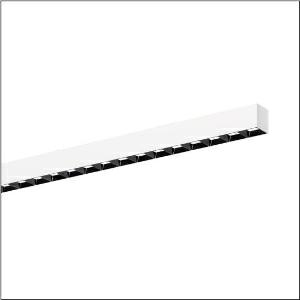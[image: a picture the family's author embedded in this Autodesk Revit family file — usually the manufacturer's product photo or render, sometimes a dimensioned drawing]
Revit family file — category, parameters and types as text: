
# Revit family: silica_r__21_51mx22da44wb_17fd
name_source: partatom
category: Lighting Fixtures
units: mm (PartAtom-declared; Revit-internal decimal feet)

## family parameters
Cut with Voids When Loaded = No
Host = Face
Light Source = No
Part Type = Normal
Room Calculation Point = No
Round Connector Dimension = Use Diameter
Shared = No

## types (1)
- --- (1 x LED, 4320 lm, 25.6 W, 4000K)
    Apparent Load = 26 VA
    CIE Flux Codes = 86 100 100 100 100
    Color Rendering = 80
    Color Temperature = 4000K
    Default Elevation = 1800 mm
    Description = Silica® 21, office luminaire, primary light control with darklight reflector, of PMMA, black, CAT 2 (L<= 3000cd/m²), light emission: direct distribution, primary light characteristic: symmetric, installation type: surface-mounted, LED, rated luminous flux: 4.320lm, luminous efficacy: 169lm/W, light colour: 840, colour temperature: 4000K, with terminal, 3+2-pole, max. 2.5mm², mains connection: 220..240V, AC, 50/60Hz, rated input power: 25.6W, luminaire housing, of aluminium, traffic white (RAL 9016), length: 1.204mm, width: 53mm, height: 53mm, protection rating (complete): IP20, insulation class (complete): insulation class I (protective earthing), certification: CE, permissible operating ambient temperature: 0..+35°C, standard: EN 50419, packaging unit: 1 piece
    Height = 0 mm  [stored 0 ft]
    Lamp = 1 x LED
    Lamp Light Flux = 4320 lm
    Lamp Power = 25.6 W
    Lamp count = 1
    Length = 1204 mm
    Luminous efficacy = 169 lm/W
    Manufacturer = Siteco
    ModVariant = No
    Model = 51MX22DA44WB
    Mounting Place = Ceiling
    Mounting Type = Recessed
    Number of Poles = 1
    OnlyDefault = Yes
    Power Factor = 1
    Product Name = Silica® 21
    Product group = office luminaire | ceiling recessed
    ProductGroupID = 401
    Protection Class = Protection class I
    Protection Degree = IP 20
    RLX_Detail_Level = 1
    RLX_Emergency_Light_Flux = 0 lm
    RLX_Emergency_Type = 0
    RLX_Emergency_Type_DB = No
    RlxData = <blob elided: 41321 chars, md5=b3e29b7a>
    Socket = socket
    Standby Power = 0 W
    System Light Flux = 4320 lm
    System Power = 26 W
    Type Comments = factory setting: luminous flux: 100 % | dim-lin: 254 | 367 mA
    Type Image = l_1313592.jpg
    URL = http://relux.com
    VarID = @adj_074659
    Voltage = 0 V
    Weight = 0.00 kg
    Width = 53 mm

note: [stored X ft] marks values corroborated as IEEE doubles in the binary element streams (Revit-internal decimal feet)

## geometry (parser evidence)
native form markers: Blend x4, Sweep x10
no freeform markers — native parametric forms only
